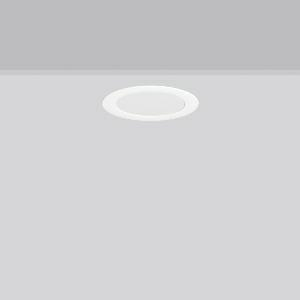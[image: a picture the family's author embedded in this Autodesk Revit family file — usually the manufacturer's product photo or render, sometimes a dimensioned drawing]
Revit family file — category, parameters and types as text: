
# Revit family: toledo_flat_round_e_672229_002_20fd
name_source: partatom
category: Lighting Fixtures
units: mm (PartAtom-declared; Revit-internal decimal feet)

## family parameters
Cut with Voids When Loaded = No
Host = Face
Light Source = No
Part Type = Normal
Room Calculation Point = No
Round Connector Dimension = Use Diameter
Shared = No

## types (1)
- TOLEDO FLAT round E (1 x LED Modul 830, 780 lm, 3000)
    Apparent Load = 8 VA
    CIE Flux Codes = 47 79 96 100 100
    Color Rendering = 80
    Color Temperature = 3000
    Default Elevation = 1800 mm
    Description = Series: TOLEDO FLAT round
Ultra thin recessed downlight. For escape route illumination. Housing: die-cast aluminium, powder-coated. Lightguide and diffuser made of non-yellowing plastic (PMMA). Diffuser opal matt plastic. Ceiling installation with spring system. Including separate LED converter with connecting cable 250 mm. Suitable for connection to central battery systems. External driver with simple plug-in locking system. 
Colour: white
Diameter: 190 mm
Height: 2.5 mm
Cut-out diameter: 170 mm
Recess height: 35 mm
Luminaire: recess height: 31-51 mm
Weight: 413 g
Operating mode: maintained power mode
Lamp: LED
Socket: without socket
Colour temperature: 3000K
Colour rendering index (CRI): 80
System power: 7.7 W
Rated luminous flux: 780 lm
Luminous flux, emergency: 780 lm
System power, emergency: 7.7 W
Control gear: Regulated power supply
Protection class: II
Type of protection: IP 54
    Height = 0 mm  [stored 0 ft]
    Lamp = 1 x LED Modul 830
    Lamp Light Flux = 780 lm
    Lamp count = 1
    Length = 190 mm  [stored 0.62336 ft]
    Lifetime = 50000 h
    Luminous efficacy = 101 lm/W
    Manufacturer = RZB
    ModVariant = No
    Model = 672229.002
    Mounting Place = Ceiling
    Mounting Type = Recessed
    Number of Poles = 1
    OnlyDefault = Yes
    Power Factor = 1
    Product Name = TOLEDO FLAT round E
    Product group = Recessed downlights
    ProductGroupID = 402
    Protection Class = Protection class II
    Protection Degree = IP 40
    RLX_Detail_Level = 1
    RLX_Emergency_Light_Flux = 780 lm
    RLX_Emergency_Type = 3
    RLX_Emergency_Type_DB = Yes
    RlxData = <blob elided: 29469 chars, md5=96b772df>
    Socket = socket
    Standby Power = 0 W
    System Light Flux = 780 lm
    System Power = 8 W
    Type Comments = Product without accessories
    Type Image = 901452.002.jpg
    URL = http://relux.com
    VarID = ---
    Voltage = 230 V
    Voltage Range = 220-240 V
    Weight = 0.00 kg
    Width = 0 mm  [stored 0 ft]

note: [stored X ft] marks values corroborated as IEEE doubles in the binary element streams (Revit-internal decimal feet)

## geometry (parser evidence)
native form markers: Blend x4, Sweep x10
no freeform markers — native parametric forms only
